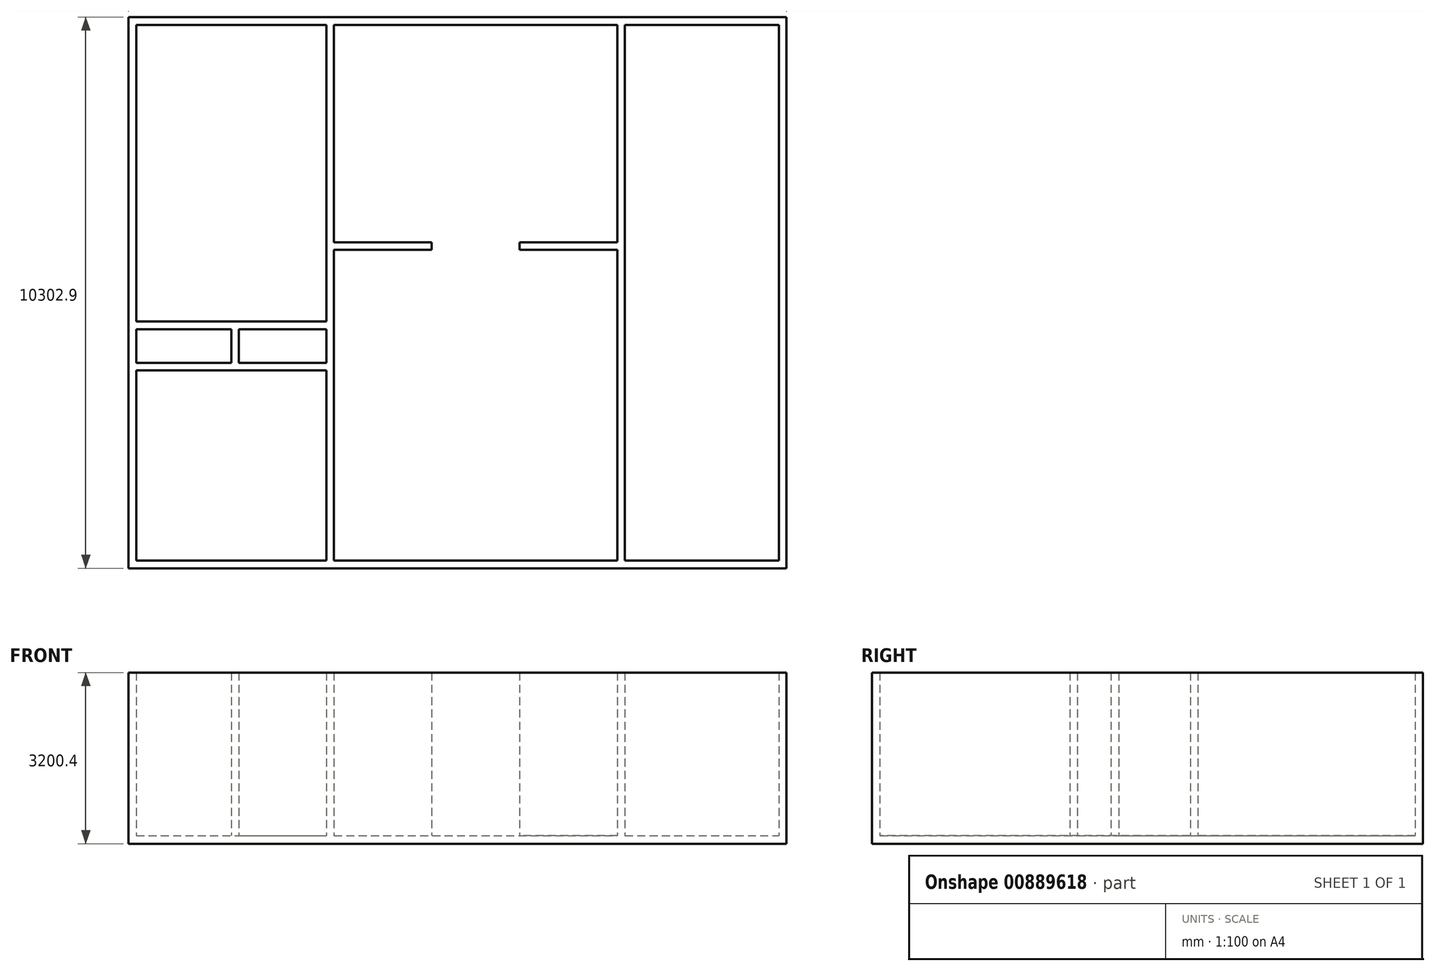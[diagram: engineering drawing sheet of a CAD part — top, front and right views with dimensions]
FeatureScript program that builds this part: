
annotation { "Feature Type Name" : "Feature", "Feature Type Description" : "" }
export const myFeature = defineFeature(function(context is Context, id is Id, definition is map)
    precondition{}
    {
        {
            var Q0;
            Q0=qCreatedBy(makeId("Top.planeOp"),FACE);
            var sketch = newSketch(context, id + "F0", { "sketchPlane" : qUnion([Q0])});
            skLineSegment(sketch, "E0.bottom", {"start": v(0, -10302.88) * mm, "end": v(12306.3, -10302.88) * mm});
            skLineSegment(sketch, "E0.top", {"start": v(0, 0) * mm, "end": v(12306.3, 0) * mm});
            skLineSegment(sketch, "E0.left", {"start": v(0, -10302.88) * mm, "end": v(0, 0) * mm});
            skLineSegment(sketch, "E0.right", {"start": v(12306.3, -10302.88) * mm, "end": v(12306.3, 0) * mm});
            skSolve(sketch);
        }
        {
            var Q0;
            Q0=makeQuery(id+"F0.imprint","IMPRINT",FACE,{"disambiguationData":[TD([[makeQuery(id+"F0.imprint","IMPRINT",EDGE,{"derivedFrom":sQuery(id+"F0.wireOp",EDGE,"E0.bottom")}),1.0]])]});
            extrude(context, id + "F1", {"entities" : qUnion([Q0]), "depth" : 152.4 * mm, "offsetDistance" : 25.4 * mm});
        }
        {
            var Q0;
            Q0=makeQuery(id+"F1.opExtrude","CAP_FACE",FACE,{"disambiguationData":[OSD([sQuery(id+"F0.wireOp",EDGE,"E0.bottom"),sQuery(id+"F0.wireOp",EDGE,"E0.top"),sQuery(id+"F0.wireOp",EDGE,"E0.left"),sQuery(id+"F0.wireOp",EDGE,"E0.right")])],"isStart":false});
            var sketch = newSketch(context, id + "F2", { "sketchPlane" : qUnion([Q0])});
            skLineSegment(sketch, "E1.0", {"start": v(0, -10302.88) * mm, "end": v(0, 0) * mm});
            skLineSegment(sketch, "E1.1", {"start": v(0, -10302.88) * mm, "end": v(12306.3, -10302.88) * mm});
            skLineSegment(sketch, "E1.2", {"start": v(12306.3, -10302.88) * mm, "end": v(12306.3, 0) * mm});
            skLineSegment(sketch, "E1.3", {"start": v(0, 0) * mm, "end": v(12306.3, 0) * mm});
            skLineSegment(sketch, "E2.0", {"start": v(142.88, -10160) * mm, "end": v(142.88, -6604) * mm});
            skLineSegment(sketch, "E2.1", {"start": v(142.88, -10160) * mm, "end": v(3698.88, -10160) * mm});
            skLineSegment(sketch, "E2.2", {"start": v(12163.43, -10160) * mm, "end": v(12163.43, -142.88) * mm});
            skLineSegment(sketch, "E2.3", {"start": v(142.88, -142.88) * mm, "end": v(3698.88, -142.88) * mm});
            skLineSegment(sketch, "E3", {"start": v(9283.7, -10160) * mm, "end": v(9283.7, -142.88) * mm});
            skLineSegment(sketch, "E4", {"start": v(9140.83, -10160) * mm, "end": v(9140.83, -4349.75) * mm});
            skLineSegment(sketch, "E5.trimOffspring", {"start": v(9283.7, -142.88) * mm, "end": v(12163.43, -142.88) * mm});
            skLineSegment(sketch, "E6.trimOffspring", {"start": v(9283.7, -10160) * mm, "end": v(12163.43, -10160) * mm});
            skLineSegment(sketch, "E7", {"start": v(3698.88, -10160) * mm, "end": v(3698.88, -6604) * mm});
            skLineSegment(sketch, "E8", {"start": v(3841.75, -142.87) * mm, "end": v(3841.75, -4206.88) * mm});
            skLineSegment(sketch, "E9.trimOffspring", {"start": v(3841.75, -10160) * mm, "end": v(9140.83, -10160) * mm});
            skLineSegment(sketch, "E10.trimOffspring", {"start": v(3841.75, -142.88) * mm, "end": v(9140.83, -142.88) * mm});
            skLineSegment(sketch, "E11", {"start": v(142.88, -6604) * mm, "end": v(3698.88, -6604) * mm});
            skLineSegment(sketch, "E12", {"start": v(142.88, -6461.12) * mm, "end": v(1920.88, -6461.12) * mm});
            skLineSegment(sketch, "E13.trimOffspring", {"start": v(3698.88, -6461.12) * mm, "end": v(3698.88, -5832.47) * mm});
            skLineSegment(sketch, "E14.trimOffspring", {"start": v(142.88, -6461.12) * mm, "end": v(142.88, -5832.47) * mm});
            skLineSegment(sketch, "E15", {"start": v(142.88, -5689.6) * mm, "end": v(3698.88, -5689.6) * mm});
            skLineSegment(sketch, "E16", {"start": v(142.88, -5832.47) * mm, "end": v(1920.88, -5832.47) * mm});
            skLineSegment(sketch, "E17.trimOffspring", {"start": v(142.88, -5689.6) * mm, "end": v(142.88, -142.88) * mm});
            skLineSegment(sketch, "E18.trimOffspring", {"start": v(3698.88, -5689.6) * mm, "end": v(3698.88, -142.87) * mm});
            skLineSegment(sketch, "E19", {"start": v(1920.88, -6461.12) * mm, "end": v(1920.88, -5832.47) * mm});
            skLineSegment(sketch, "E20", {"start": v(2063.75, -6461.12) * mm, "end": v(2063.75, -5832.47) * mm});
            skLineSegment(sketch, "E21.trimOffspring", {"start": v(2063.75, -6461.12) * mm, "end": v(3698.88, -6461.12) * mm});
            skLineSegment(sketch, "E22.trimOffspring", {"start": v(2063.75, -5832.47) * mm, "end": v(3698.88, -5832.47) * mm});
            skLineSegment(sketch, "E23.bottom", {"start": v(3841.75, -4349.75) * mm, "end": v(5670.55, -4349.75) * mm});
            skLineSegment(sketch, "E23.top", {"start": v(3841.75, -4206.88) * mm, "end": v(5670.55, -4206.88) * mm});
            skLineSegment(sketch, "E23.right", {"start": v(5670.55, -4349.75) * mm, "end": v(5670.55, -4206.88) * mm});
            skLineSegment(sketch, "E24.bottom", {"start": v(9140.83, -4349.75) * mm, "end": v(7312.03, -4349.75) * mm});
            skLineSegment(sketch, "E24.top", {"start": v(9140.83, -4206.87) * mm, "end": v(7312.03, -4206.87) * mm});
            skLineSegment(sketch, "E24.right", {"start": v(7312.03, -4349.75) * mm, "end": v(7312.03, -4206.87) * mm});
            skLineSegment(sketch, "E25.trimOffspring", {"start": v(3841.75, -4349.75) * mm, "end": v(3841.75, -10160) * mm});
            skLineSegment(sketch, "E26.trimOffspring", {"start": v(9140.83, -4206.87) * mm, "end": v(9140.83, -142.87) * mm});
            skSolve(sketch);
        }
        {
            var Q0;
            Q0=makeQuery(id+"F2.imprint","IMPRINT",FACE,{"disambiguationData":[TD([[makeQuery(id+"F2.imprint","IMPRINT",EDGE,{"derivedFrom":sQuery(id+"F2.wireOp",EDGE,"E1.0")}),-1.0]])]});
            extrude(context, id + "F3", {"entities" : qUnion([Q0]), "operationType" : NewBodyOperationType.ADD, "depth" : 3048 * mm, "offsetDistance" : 25.4 * mm});
        }
    });
